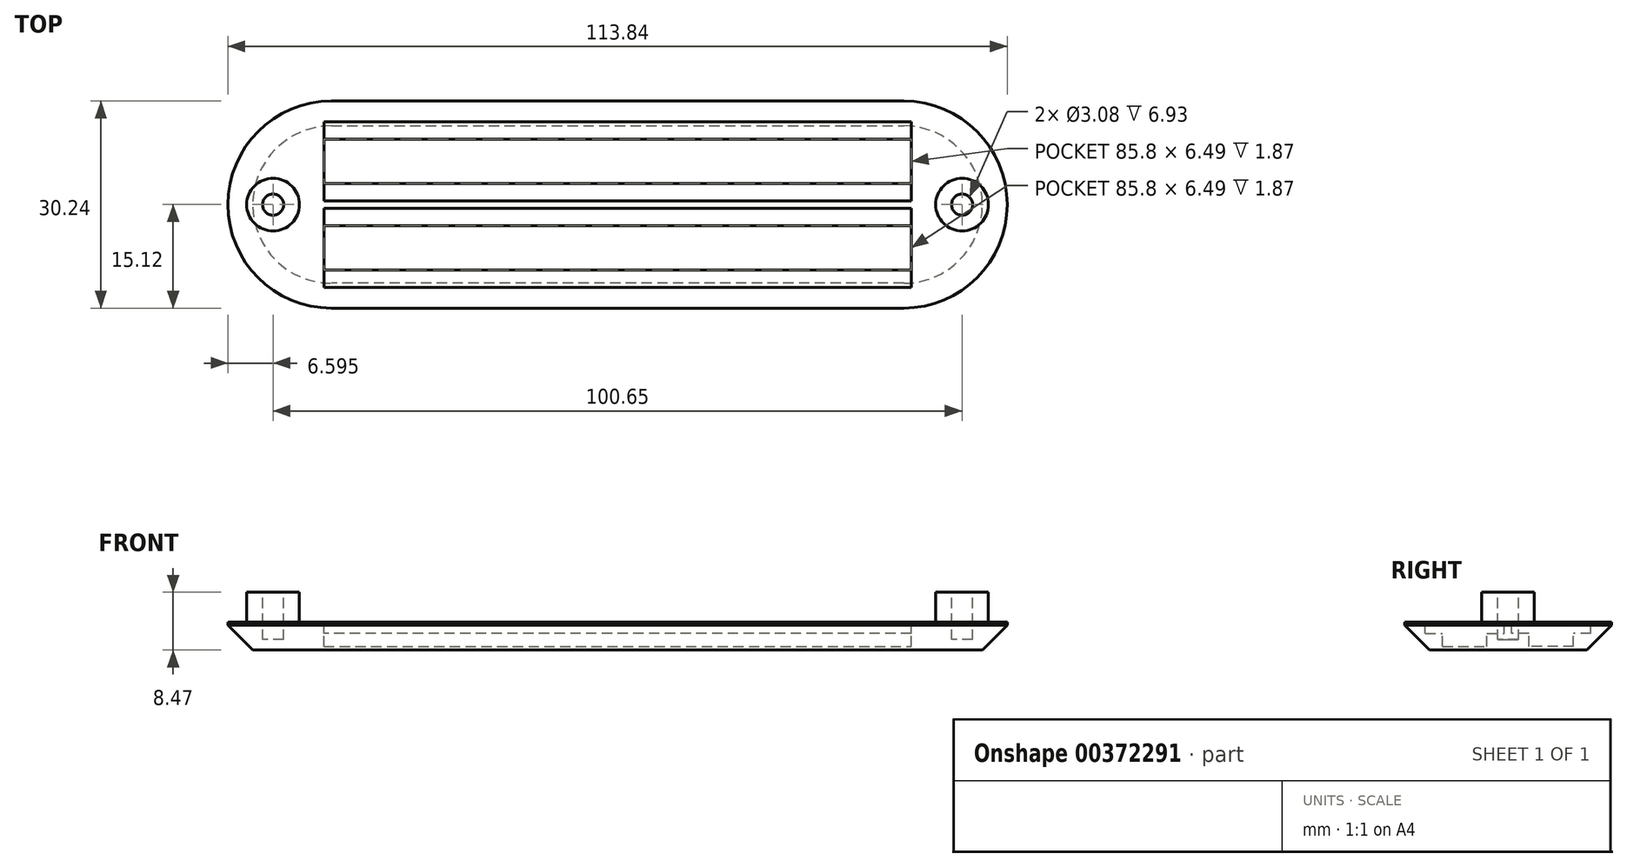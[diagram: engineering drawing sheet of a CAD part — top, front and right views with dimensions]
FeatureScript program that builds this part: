
annotation { "Feature Type Name" : "Feature", "Feature Type Description" : "" }
export const myFeature = defineFeature(function(context is Context, id is Id, definition is map)
    precondition{}
    {
        {
            var Q0;
            Q0=qCreatedBy(makeId("Top.planeOp"),FACE);
            var sketch = newSketch(context, id + "F0", { "sketchPlane" : qUnion([Q0])});
            skLineSegment(sketch, "E0.bottom", {"start": v(38, 13.75) * mm, "end": v(-38, 13.75) * mm});
            skLineSegment(sketch, "E0.top", {"start": v(38, -13.75) * mm, "end": v(-38, -13.75) * mm});
            skLineSegment(sketch, "E0.left", {"start": v(38, 13.75) * mm, "end": v(38, -13.75) * mm});
            skLineSegment(sketch, "E0.right", {"start": v(-38, 13.75) * mm, "end": v(-38, -13.75) * mm});
            skPoint(sketch, "E0.middle", {"position": v(0, 0) * mm});
            skCircle(sketch, "E1", {"center": v(-38, 0) * mm, "radius": 13.75 * mm});
            skCircle(sketch, "E2", {"center": v(38, 0) * mm, "radius": 13.75 * mm});
            skSolve(sketch);
        }
        {
            var Q0;
            {var subQ0=sQuery(id+"F0.wireOp",EDGE,"E0.bottom");Q0=makeQuery(id+"F0.imprint","IMPRINT",FACE,{"disambiguationData":[TD([[makeQuery(id+"F0.imprint","IMPRINT",EDGE,{"derivedFrom":subQ0}),1.0]])]});}
            var Q1;
            {var subQ0=sQuery(id+"F0.wireOp",EDGE,"E0.right");Q1=makeQuery(id+"F0.imprint","IMPRINT",FACE,{"disambiguationData":[TD([[makeQuery(id+"F0.imprint","IMPRINT",EDGE,{"derivedFrom":subQ0}),1.0]])]});}
            var Q2;
            {var subQ0=sQuery(id+"F0.wireOp",EDGE,"E0.right");Q2=makeQuery(id+"F0.imprint","IMPRINT",FACE,{"disambiguationData":[TD([[makeQuery(id+"F0.imprint","IMPRINT",EDGE,{"derivedFrom":subQ0}),-1.0]])]});}
            var Q3;
            {var subQ0=sQuery(id+"F0.wireOp",EDGE,"E0.left");Q3=makeQuery(id+"F0.imprint","IMPRINT",FACE,{"disambiguationData":[TD([[makeQuery(id+"F0.imprint","IMPRINT",EDGE,{"derivedFrom":subQ0}),-1.0]])]});}
            var Q4;
            {var subQ0=sQuery(id+"F0.wireOp",EDGE,"E0.left");Q4=makeQuery(id+"F0.imprint","IMPRINT",FACE,{"disambiguationData":[TD([[makeQuery(id+"F0.imprint","IMPRINT",EDGE,{"derivedFrom":subQ0}),1.0]])]});}
            extrude(context, id + "F1", {"entities" : qUnion([Q0, Q1, Q2, Q3, Q4]), "depth" : 3.7 * mm});
        }
        {
            var Q0;
            Q0=makeQuery(id+"F1.opExtrude","CAP_FACE",FACE,{"disambiguationData":[OSD([sQuery(id+"F0.wireOp",EDGE,"E0.bottom"),sQuery(id+"F0.wireOp",EDGE,"E0.top"),sQuery(id+"F0.wireOp",EDGE,"E1"),sQuery(id+"F0.wireOp",EDGE,"E2")])],"isStart":false});
            var sketch = newSketch(context, id + "F2", { "sketchPlane" : qUnion([Q0])});
            skPoint(sketch, "E3", {"position": v(39, 0.5) * mm});
            skPoint(sketch, "E4", {"position": v(39, 11) * mm});
            skPoint(sketch, "E5", {"position": v(-45.75, 0) * mm});
            skPoint(sketch, "E5.positionSnap0", {"position": v(-51.75, 0) * mm});
            skCircle(sketch, "E6", {"center": v(-45.75, 0) * mm, "radius": 3.5 * mm});
            skPoint(sketch, "E7", {"position": v(-39, 0.5) * mm});
            skLineSegment(sketch, "E8.bottom", {"start": v(39, 11) * mm, "end": v(-39, 11) * mm});
            skLineSegment(sketch, "E8.top", {"start": v(39, 0.5) * mm, "end": v(-39, 0.5) * mm});
            skLineSegment(sketch, "E8.left", {"start": v(39, 11) * mm, "end": v(39, 0.5) * mm});
            skLineSegment(sketch, "E8.right", {"start": v(-39, 11) * mm, "end": v(-39, 0.5) * mm});
            skLineSegment(sketch, "E9.MirrorCS", {"start": v(-39, -11) * mm, "end": v(-39, -0.5) * mm});
            skLineSegment(sketch, "E10.MirrorCS", {"start": v(39, -0.5) * mm, "end": v(-39, -0.5) * mm});
            skLineSegment(sketch, "E11.MirrorCS", {"start": v(39, -11) * mm, "end": v(-39, -11) * mm});
            skLineSegment(sketch, "E12.MirrorCS", {"start": v(39, -11) * mm, "end": v(39, -0.5) * mm});
            skPoint(sketch, "E13.positionSnap0", {"position": v(39, 5.75) * mm});
            skPoint(sketch, "E14", {"position": v(39, 8.7) * mm});
            skPoint(sketch, "E15", {"position": v(-39, 2.8) * mm});
            skLineSegment(sketch, "E16.bottom", {"start": v(-39, 2.8) * mm, "end": v(39, 2.8) * mm});
            skLineSegment(sketch, "E16.top", {"start": v(-39, 8.7) * mm, "end": v(39, 8.7) * mm});
            skLineSegment(sketch, "E16.left", {"start": v(-39, 2.8) * mm, "end": v(-39, 8.7) * mm});
            skLineSegment(sketch, "E16.right", {"start": v(39, 2.8) * mm, "end": v(39, 8.7) * mm});
            skLineSegment(sketch, "E17.MirrorCS", {"start": v(-39, -2.8) * mm, "end": v(39, -2.8) * mm});
            skLineSegment(sketch, "E18.MirrorCS", {"start": v(-39, -8.7) * mm, "end": v(39, -8.7) * mm});
            skCircle(sketch, "E19", {"center": v(45.75, 0) * mm, "radius": 3.5 * mm});
            skPoint(sketch, "E20", {"position": v(0, 0.5) * mm});
            skPoint(sketch, "E21", {"position": v(39, 0) * mm});
            skPoint(sketch, "E22", {"position": v(51.75, 0) * mm});
            skPoint(sketch, "E23", {"position": v(-39, 0) * mm});
            skSolve(sketch);
        }
        {
            var Q0;
            {var subQ0=sQuery(id+"F2.wireOp",EDGE,"E8.bottom");Q0=makeQuery(id+"F2.imprint","IMPRINT",FACE,{"disambiguationData":[TD([[makeQuery(id+"F2.imprint","IMPRINT",EDGE,{"derivedFrom":subQ0}),1.0]])]});}
            var Q1;
            {var subQ0=sQuery(id+"F2.wireOp",EDGE,"E8.top");Q1=makeQuery(id+"F2.imprint","IMPRINT",FACE,{"disambiguationData":[TD([[makeQuery(id+"F2.imprint","IMPRINT",EDGE,{"derivedFrom":subQ0}),-1.0]])]});}
            var Q2;
            {var subQ0=sQuery(id+"F2.wireOp",EDGE,"E10.MirrorCS");Q2=makeQuery(id+"F2.imprint","IMPRINT",FACE,{"disambiguationData":[TD([[makeQuery(id+"F2.imprint","IMPRINT",EDGE,{"derivedFrom":subQ0}),1.0]])]});}
            var Q3;
            {var subQ0=sQuery(id+"F2.wireOp",EDGE,"E11.MirrorCS");Q3=makeQuery(id+"F2.imprint","IMPRINT",FACE,{"disambiguationData":[TD([[makeQuery(id+"F2.imprint","IMPRINT",EDGE,{"derivedFrom":subQ0}),-1.0]])]});}
            extrude(context, id + "F3", {"entities" : qUnion([Q0, Q1, Q2, Q3]), "operationType" : NewBodyOperationType.REMOVE, "oppositeDirection" : true, "depth" : 1.5 * mm});
        }
        {
            var Q0;
            Q0=makeQuery(id+"F2.imprint","IMPRINT",FACE,{"disambiguationData":[TD([[makeQuery(id+"F2.imprint","IMPRINT",EDGE,{"derivedFrom":sQuery(id+"F2.wireOp",EDGE,"E16.bottom")}),1.0]])]});
            var Q1;
            {var subQ0=sQuery(id+"F2.wireOp",EDGE,"E17.MirrorCS");Q1=makeQuery(id+"F2.imprint","IMPRINT",FACE,{"disambiguationData":[TD([[makeQuery(id+"F2.imprint","IMPRINT",EDGE,{"derivedFrom":subQ0}),-1.0]])]});}
            extrude(context, id + "F4", {"entities" : qUnion([Q0, Q1]), "operationType" : NewBodyOperationType.REMOVE, "oppositeDirection" : true, "depth" : 3.2 * mm});
        }
        {
            var Q0;
            Q0=makeQuery(id+"F2.imprint","IMPRINT",FACE,{"disambiguationData":[TD([[makeQuery(id+"F2.imprint","IMPRINT",EDGE,{"derivedFrom":sQuery(id+"F2.wireOp",EDGE,"E19")}),1.0]])]});
            var Q1;
            Q1=makeQuery(id+"F2.imprint","IMPRINT",FACE,{"disambiguationData":[TD([[makeQuery(id+"F2.imprint","IMPRINT",EDGE,{"derivedFrom":sQuery(id+"F2.wireOp",EDGE,"E6")}),1.0]])]});
            extrude(context, id + "F5", {"entities" : qUnion([Q0, Q1]), "operationType" : NewBodyOperationType.ADD, "depth" : 4 * mm});
        }
        {
            var Q0;
            Q0=makeQuery(id+"F5.opExtrude","CAP_FACE",FACE,{"disambiguationData":[OSD([sQuery(id+"F2.wireOp",EDGE,"E19")])],"isStart":false});
            var sketch = newSketch(context, id + "F6", { "sketchPlane" : qUnion([Q0])});
            skCircle(sketch, "E24", {"center": v(45.75, 0) * mm, "radius": 1.4 * mm});
            skSolve(sketch);
        }
        {
            var Q0;
            Q0=makeQuery(id+"F6.imprint","IMPRINT",FACE,{"disambiguationData":[TD([[makeQuery(id+"F6.imprint","IMPRINT",EDGE,{"derivedFrom":sQuery(id+"F6.wireOp",EDGE,"E24")}),1.0]])]});
            extrude(context, id + "F7", {"entities" : qUnion([Q0]), "operationType" : NewBodyOperationType.REMOVE, "oppositeDirection" : true, "depth" : 6.3 * mm});
        }
        {
            var Q0;
            Q0=makeQuery(id+"F5.opExtrude","CAP_FACE",FACE,{"disambiguationData":[OSD([sQuery(id+"F2.wireOp",EDGE,"E6")])],"isStart":false});
            var sketch = newSketch(context, id + "F8", { "sketchPlane" : qUnion([Q0])});
            skCircle(sketch, "E25", {"center": v(-45.75, 0) * mm, "radius": 1.4 * mm});
            skSolve(sketch);
        }
        {
            var Q0;
            Q0=makeQuery(id+"F8.imprint","IMPRINT",FACE,{"disambiguationData":[TD([[makeQuery(id+"F8.imprint","IMPRINT",EDGE,{"derivedFrom":sQuery(id+"F8.wireOp",EDGE,"E25")}),1.0]])]});
            extrude(context, id + "F9", {"entities" : qUnion([Q0]), "operationType" : NewBodyOperationType.REMOVE, "oppositeDirection" : true, "depth" : 6.3 * mm});
        }
        {
            var Q0;
            Q0=makeQuery(id+"F1.opExtrude","CAP_EDGE",EDGE,{"disambiguationData":[OSD([sQuery(id+"F0.wireOp",EDGE,"E0.bottom")])],"isStart":true});
            chamfer(context, id + "F10", {"entities" : qUnion([Q0]), "width" : 3.3 * mm, "tangentPropagation" : true});
        }
        {
            var Q0;
            Q0=makeQuery(id+"F1.opExtrude","SWEPT_BODY",BODY,{"disambiguationData":[OSD([sQuery(id+"F0.wireOp",EDGE,"E0.bottom"),sQuery(id+"F0.wireOp",EDGE,"E0.top"),sQuery(id+"F0.wireOp",EDGE,"E1"),sQuery(id+"F0.wireOp",EDGE,"E2")])]});
            var Q1;
            Q1=qCreatedBy(makeId("Origin.pointOp"),VERTEX);
            transform(context, id + "F11", {"entities" : qUnion([Q0]), "transformType" : TransformType.SCALE_UNIFORMLY, "scale" : 1.1, "scalePoint" : qUnion([Q1]), "makeCopy" : false});
        }
    });
